# Revit family: Kohler Aleo+ K-72328IN-4FP-AF Family
name_source: partatom
category: Specialty Equipment
revit_build: Autodesk Revit 2018 (Build: 20181011_1500(x64)
units: mm (PartAtom-declared; Revit-internal decimal feet)

## family parameters
Always vertical = Yes
Cut with Voids When Loaded = No
Part Type = Normal
Room Calculation Point = No
Round Connector Dimension = Use Diameter
Shared = No
Work Plane-Based = Yes

## types (1)
- Kohler Aleo+ K-72328IN-4FP-AF
    Default Elevation = 1219 mm
    Description = The Aleo+ faucet collection brings elegance into the home with its minimalist design. The thin handle of Aleo+ lavatory provides easy functionality and outstanding control. This valve trim for baths and showers features a sleek lever handle.
    Disclaimer = Although care has been taken to ensure, to the best of our knowledge, that all data and information contained herein is accurate to the extent that it relates to either matters of fact or accepted practice at the time of issue. MDFC (Pty) Ltd assumes no responsibility for any errors in, or misinterpretation of, such data and/ or information or any loss or damage arising from, or related to its use.
    Height = 166 mm  [stored 0.544619 ft]
    Length = 116 mm  [stored 0.380577 ft]
    Manufacturer = Kohler Co.
    Material = Chrome
    Model = Kohler Aleo+ K-72328IN-4FP-AF
    Telephone = 011 050 9000
    URL = www.africa.kohler.com
    Width = 113 mm  [stored 0.370735 ft]

note: [stored X ft] marks values corroborated as IEEE doubles in the binary element streams (Revit-internal decimal feet)

## geometry (parser evidence)
native form markers: Sweep x3
no freeform markers — native parametric forms only
